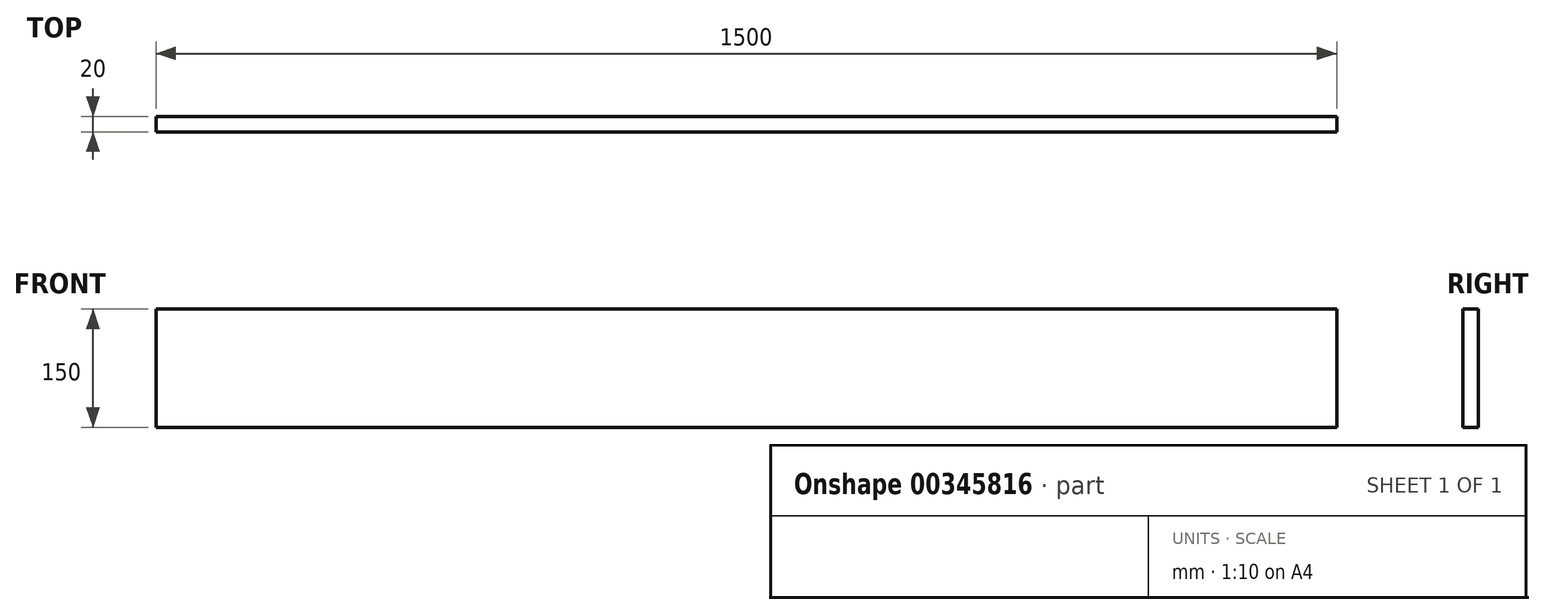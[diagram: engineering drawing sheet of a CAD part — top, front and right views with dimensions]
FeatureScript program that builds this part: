
annotation { "Feature Type Name" : "Feature", "Feature Type Description" : "" }
export const myFeature = defineFeature(function(context is Context, id is Id, definition is map)
    precondition{}
    {
        {
            var Q0;
            Q0=qCreatedBy(makeId("Front.planeOp"),FACE);
            var sketch = newSketch(context, id + "F0", { "sketchPlane" : qUnion([Q0])});
            skLineSegment(sketch, "E0.bottom", {"start": v(0, 0) * mm, "end": v(1500, 0) * mm});
            skLineSegment(sketch, "E0.top", {"start": v(0, 150) * mm, "end": v(1500, 150) * mm});
            skLineSegment(sketch, "E0.left", {"start": v(0, 0) * mm, "end": v(0, 150) * mm});
            skLineSegment(sketch, "E0.right", {"start": v(1500, 0) * mm, "end": v(1500, 150) * mm});
            skSolve(sketch);
        }
        {
            var Q0;
            Q0 = qSketchRegion(id + "F0", true);
            extrude(context, id + "F1", {"entities" : qUnion([Q0]), "depth" : 20 * mm});
        }
    });
